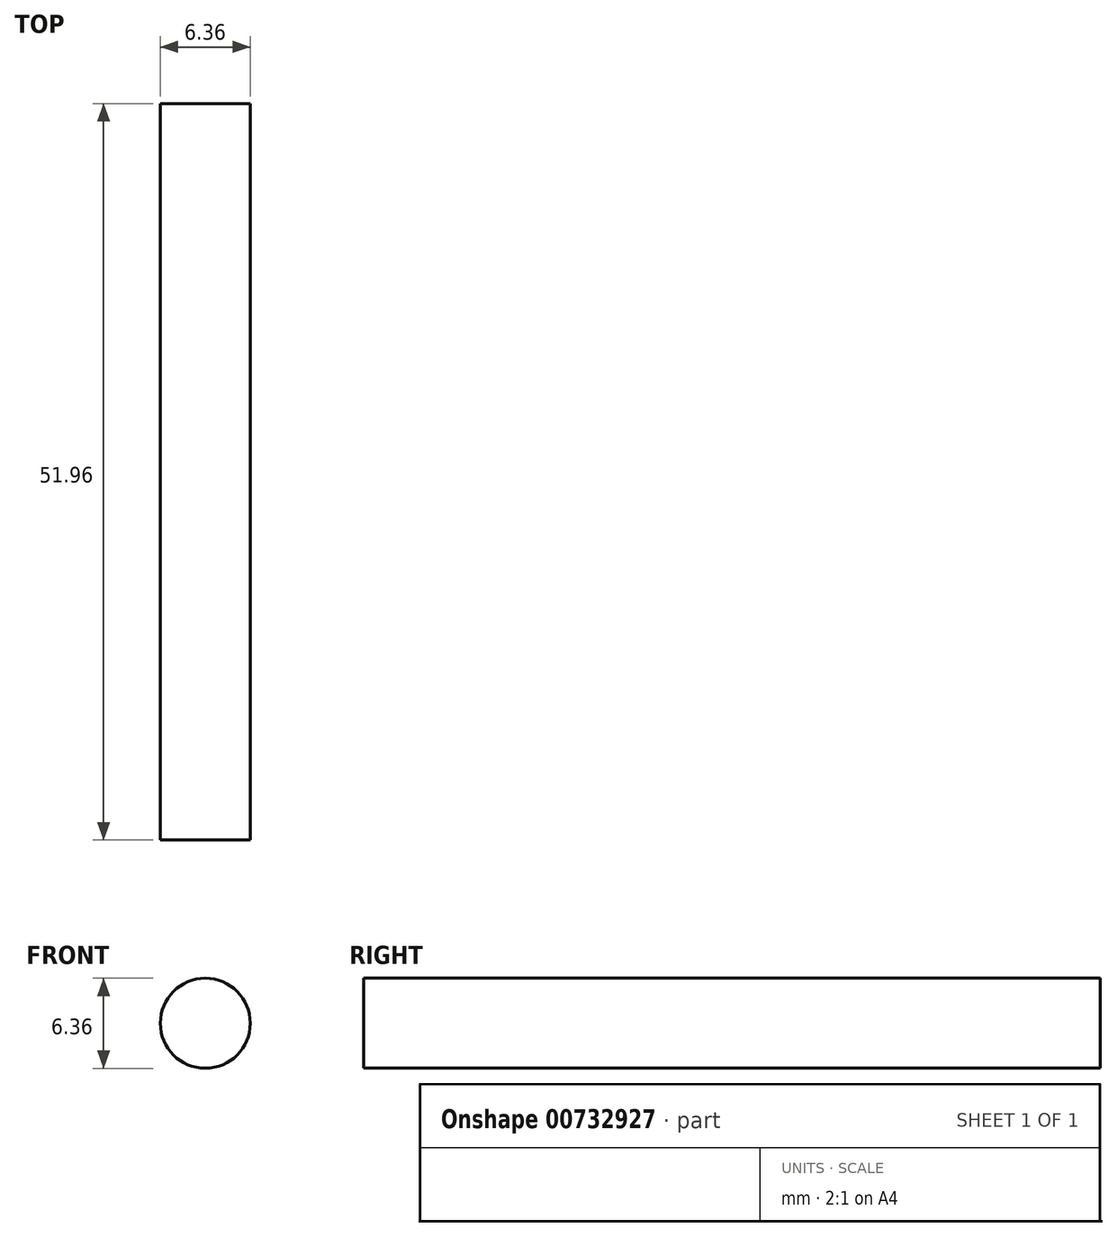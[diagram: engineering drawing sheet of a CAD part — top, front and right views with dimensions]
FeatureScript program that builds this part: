
annotation { "Feature Type Name" : "Feature", "Feature Type Description" : "" }
export const myFeature = defineFeature(function(context is Context, id is Id, definition is map)
    precondition{}
    {
        {
            var Q0;
            Q0=qCreatedBy(makeId("Front.planeOp"),FACE);
            var sketch = newSketch(context, id + "F0", { "sketchPlane" : qUnion([Q0])});
            skCircle(sketch, "E0", {"center": v(0, 0) * mm, "radius": 3.17 * mm});
            skSolve(sketch);
        }
        {
            var Q0;
            Q0 = qSketchRegion(id + "F0", true);
            extrude(context, id + "F1", {"entities" : qUnion([Q0]), "depth" : 51.96 * mm, "offsetDistance" : 25 * mm});
        }
    });
